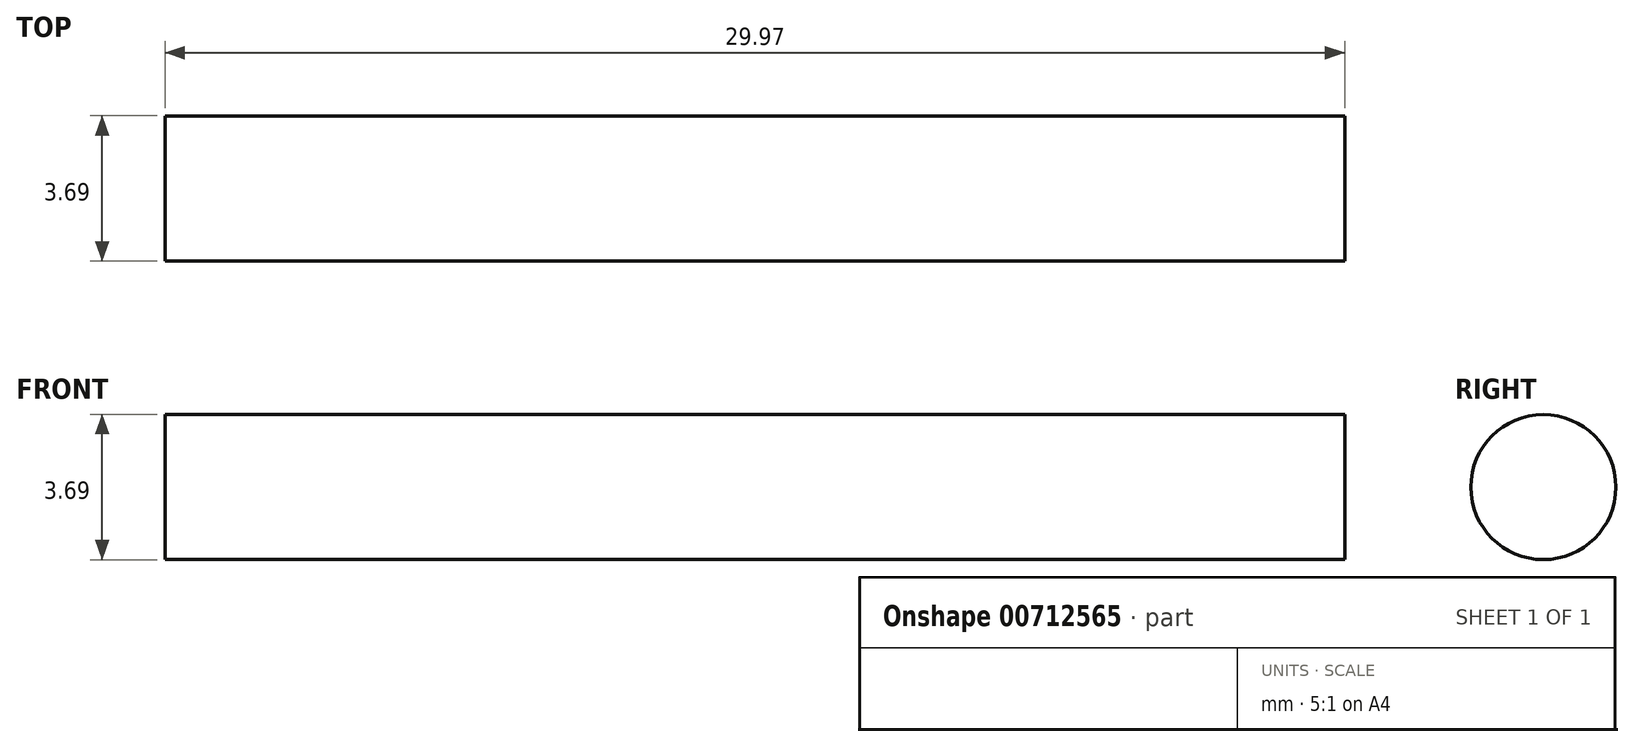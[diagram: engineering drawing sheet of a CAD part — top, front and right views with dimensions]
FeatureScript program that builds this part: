
annotation { "Feature Type Name" : "Feature", "Feature Type Description" : "" }
export const myFeature = defineFeature(function(context is Context, id is Id, definition is map)
    precondition{}
    {
        {
            var Q0;
            Q0=qCreatedBy(makeId("Right.planeOp"),FACE);
            var sketch = newSketch(context, id + "F0", { "sketchPlane" : qUnion([Q0])});
            skCircle(sketch, "E0", {"center": v(-64.32, 52.52) * mm, "radius": 1.84 * mm});
            skSolve(sketch);
        }
        {
            var Q0;
            Q0 = qSketchRegion(id + "F0", true);
            extrude(context, id + "F1", {"entities" : qUnion([Q0]), "depth" : 29.97 * mm, "offsetDistance" : 25.4 * mm});
        }
    });
